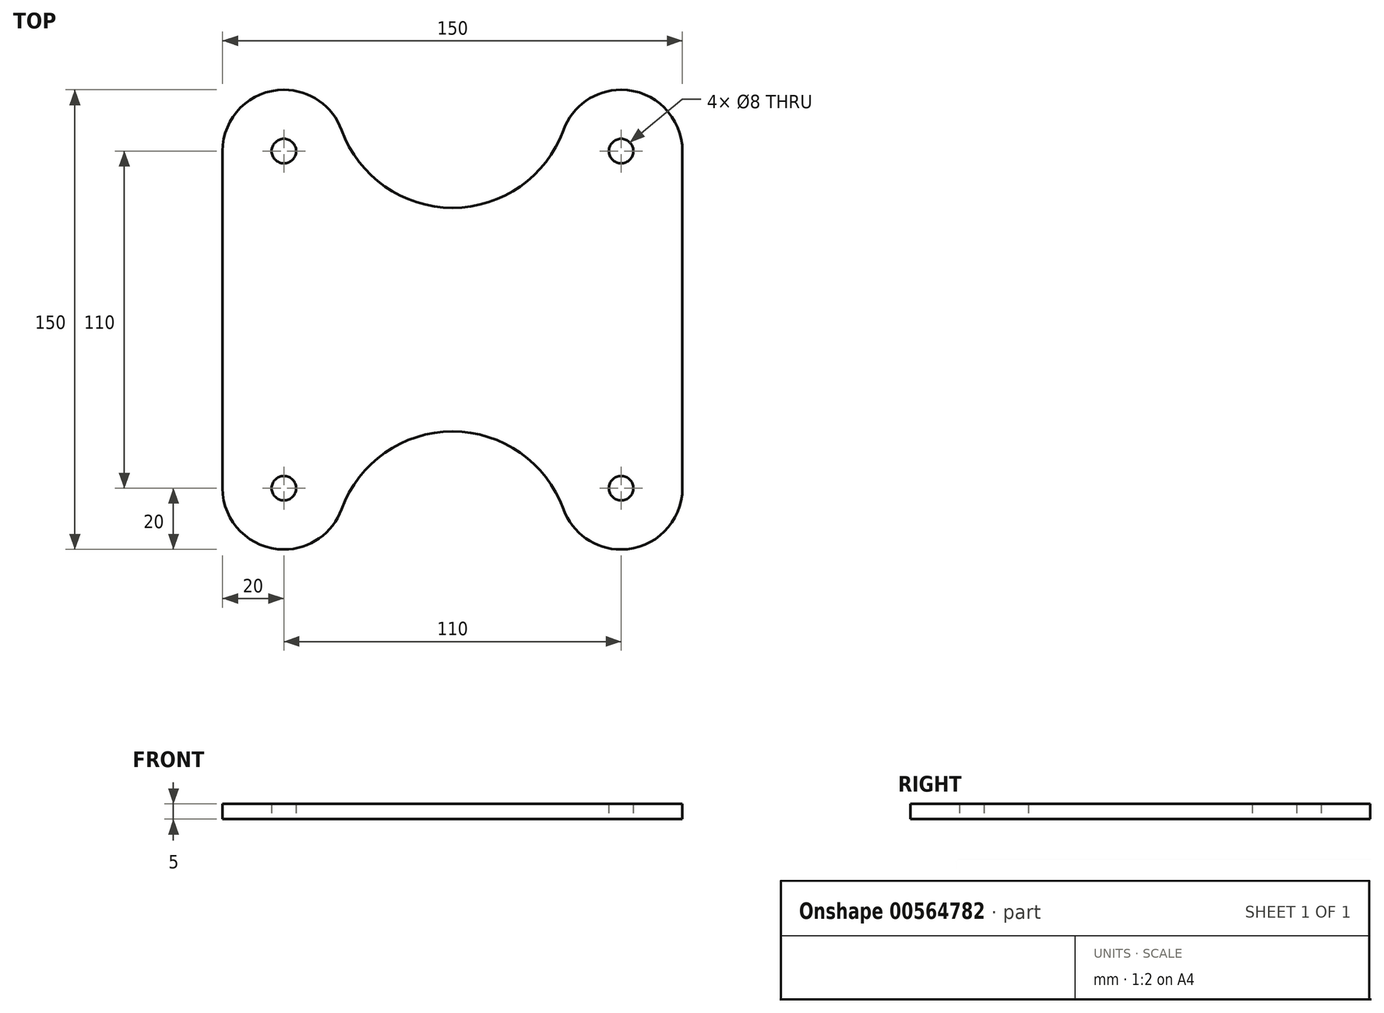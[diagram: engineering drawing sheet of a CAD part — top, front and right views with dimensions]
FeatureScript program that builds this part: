
annotation { "Feature Type Name" : "Feature", "Feature Type Description" : "" }
export const myFeature = defineFeature(function(context is Context, id is Id, definition is map)
    precondition{}
    {
        {
            var Q0;
            Q0=qCreatedBy(makeId("Top.planeOp"),FACE);
            var sketch = newSketch(context, id + "F0", { "sketchPlane" : qUnion([Q0])});
            skLineSegment(sketch, "E0.bottom", {"start": v(75, -75) * mm, "end": v(38.5, -75) * mm});
            skLineSegment(sketch, "E0.top", {"start": v(75, 75) * mm, "end": v(38.5, 75) * mm});
            skLineSegment(sketch, "E0.left", {"start": v(75, -75) * mm, "end": v(75, 75) * mm});
            skLineSegment(sketch, "E0.right", {"start": v(-75, -75) * mm, "end": v(-75, 75) * mm});
            skPoint(sketch, "E0.middle", {"position": v(0, 0) * mm});
            skArc(sketch, "E1", {"start": v(-38.5, 75) * mm, "mid": v(0, 36.5) * mm, "end": v(38.5, 75) * mm});
            skLineSegment(sketch, "E2.trimOffspring", {"start": v(-38.5, 75) * mm, "end": v(-75, 75) * mm});
            skCircle(sketch, "E3", {"center": v(-55, -55) * mm, "radius": 4 * mm});
            skCircle(sketch, "E4", {"center": v(55, -55) * mm, "radius": 4 * mm});
            skLineSegment(sketch, "E5", {"start": v(-55, -55) * mm, "end": v(-55, 75) * mm, "construction": true});
            skLineSegment(sketch, "E6", {"start": v(55, -55) * mm, "end": v(55, 75) * mm, "construction": true});
            skPoint(sketch, "E6.endSnap0", {"position": v(56.75, 75) * mm});
            skCircle(sketch, "E7", {"center": v(-55, 55) * mm, "radius": 4 * mm});
            skCircle(sketch, "E8", {"center": v(55, 55) * mm, "radius": 4 * mm});
            skArc(sketch, "E9", {"start": v(38.5, -75) * mm, "mid": v(0, -36.5) * mm, "end": v(-38.5, -75) * mm});
            skLineSegment(sketch, "E10.trimOffspring", {"start": v(-38.5, -75) * mm, "end": v(-75, -75) * mm});
            skSolve(sketch);
        }
        {
            var Q0;
            Q0=qSketchRegion(id+"F0",true);
            extrude(context, id + "F1", {"entities" : qUnion([Q0]), "endBound" : BoundingType.SYMMETRIC, "depth" : 5 * mm, "offsetDistance" : 25 * mm});
        }
        {
            var Q0;
            Q0=makeQuery(id+"F1.opExtrude","SWEPT_EDGE",EDGE,{"disambiguationData":[OSD([sQuery(id+"F0.wireOp",EDGE,"E0.bottom"),sQuery(id+"F0.wireOp",EDGE,"E0.left")])]});
            var Q1;
            Q1=makeQuery(id+"F1.opExtrude","SWEPT_EDGE",EDGE,{"disambiguationData":[OSD([sQuery(id+"F0.wireOp",EDGE,"E0.bottom"),sQuery(id+"F0.wireOp",EDGE,"E0.right")])]});
            var Q2;
            Q2=makeQuery(id+"F1.opExtrude","SWEPT_EDGE",EDGE,{"disambiguationData":[OSD([sQuery(id+"F0.wireOp",EDGE,"E0.top"),sQuery(id+"F0.wireOp",EDGE,"E0.left")])]});
            var Q3;
            Q3=makeQuery(id+"F1.opExtrude","SWEPT_EDGE",EDGE,{"disambiguationData":[OSD([sQuery(id+"F0.wireOp",EDGE,"E0.right"),sQuery(id+"F0.wireOp",EDGE,"E2.trimOffspring")])]});
            var Q4;
            Q4=makeQuery(id+"F1.opExtrude","SWEPT_EDGE",EDGE,{"disambiguationData":[OSD([sQuery(id+"F0.wireOp",EDGE,"E1"),sQuery(id+"F0.wireOp",EDGE,"E2.trimOffspring")])]});
            var Q5;
            Q5=makeQuery(id+"F1.opExtrude","SWEPT_EDGE",EDGE,{"disambiguationData":[OSD([sQuery(id+"F0.wireOp",EDGE,"E0.top"),sQuery(id+"F0.wireOp",EDGE,"E1")])]});
            var Q6;
            Q6=makeQuery(id+"F1.opExtrude","SWEPT_EDGE",EDGE,{"disambiguationData":[OSD([sQuery(id+"F0.wireOp",EDGE,"E9"),sQuery(id+"F0.wireOp",EDGE,"E10.trimOffspring")])]});
            fillet(context, id + "F2", {"entities" : qUnion([Q0, Q1, Q2, Q3, Q4, Q5, Q6]), "radius" : 20 * mm, "tangentPropagation" : true, "allowEdgeOverflow" : false});
        }
    });
